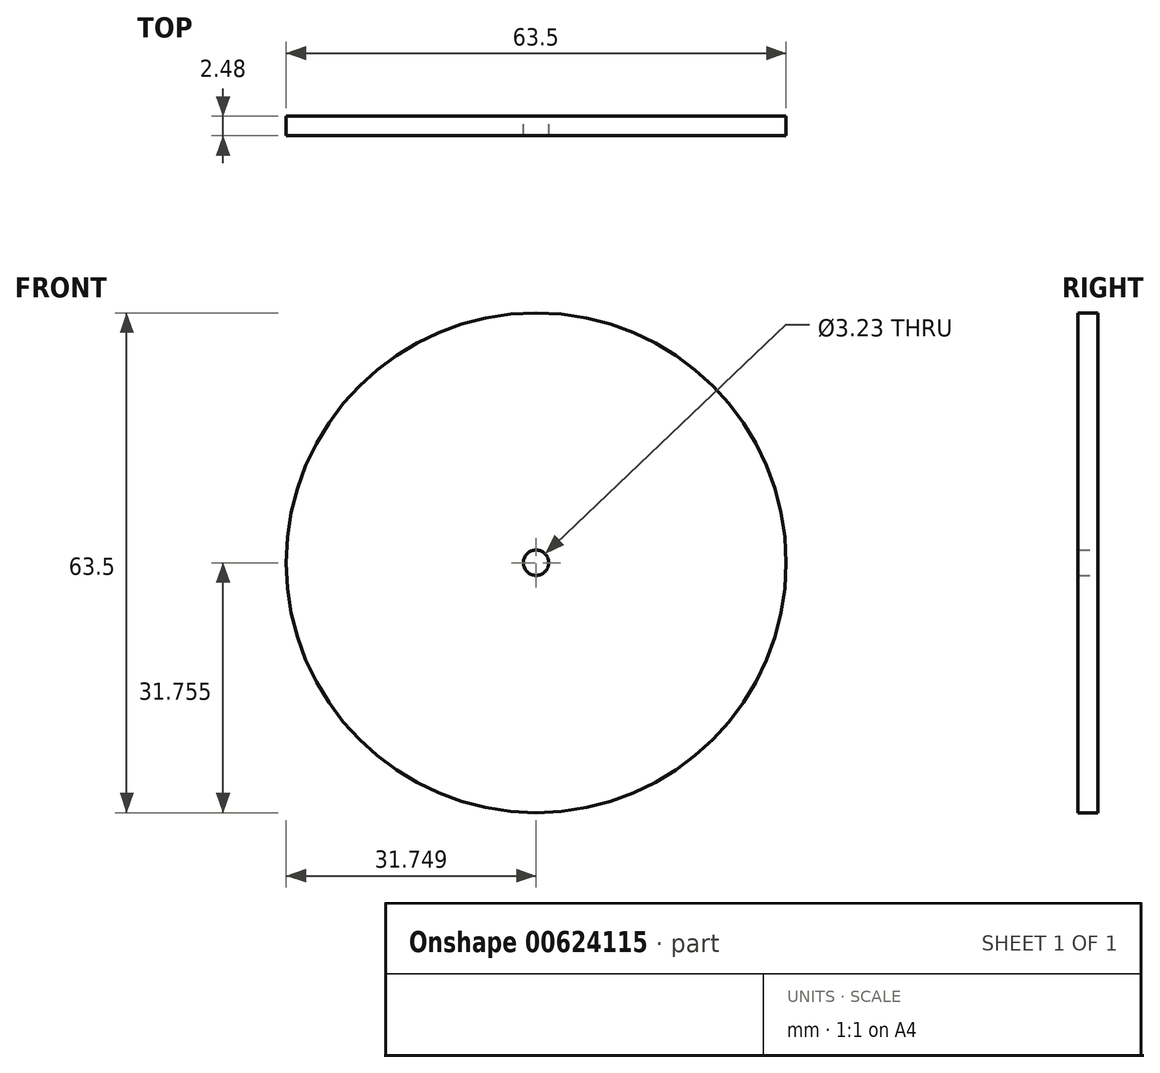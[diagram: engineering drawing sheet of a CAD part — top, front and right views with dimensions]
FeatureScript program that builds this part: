
annotation { "Feature Type Name" : "Feature", "Feature Type Description" : "" }
export const myFeature = defineFeature(function(context is Context, id is Id, definition is map)
    precondition{}
    {
        {
            var Q0;
            Q0=qCreatedBy(makeId("Front.planeOp"),FACE);
            var sketch = newSketch(context, id + "F0", { "sketchPlane" : qUnion([Q0])});
            skCircle(sketch, "E0", {"center": v(-7.56, 8.13) * mm, "radius": 31.75 * mm});
            skCircle(sketch, "E1", {"center": v(-7.56, 8.13) * mm, "radius": 1.61 * mm});
            skSolve(sketch);
        }
        {
            var Q0;
            Q0 = qSketchRegion(id + "F0", true);
            extrude(context, id + "F1", {"entities" : qUnion([Q0]), "endBound" : BoundingType.SYMMETRIC, "depth" : 2.5 * mm, "offsetDistance" : 25.4 * mm});
        }
    });
